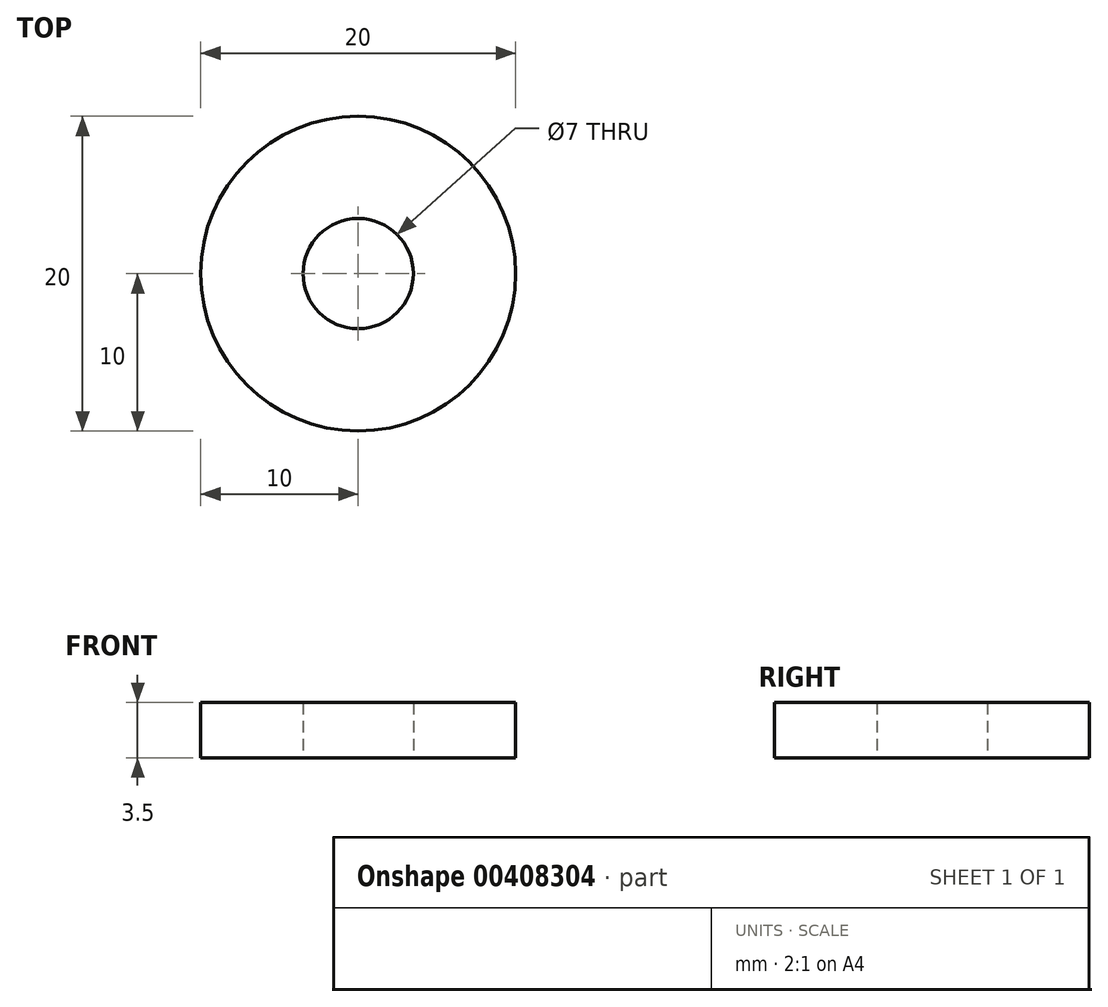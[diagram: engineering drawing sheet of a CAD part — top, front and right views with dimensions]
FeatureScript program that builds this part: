
annotation { "Feature Type Name" : "Feature", "Feature Type Description" : "" }
export const myFeature = defineFeature(function(context is Context, id is Id, definition is map)
    precondition{}
    {
        {
            var Q0;
            Q0=qCreatedBy(makeId("Top.planeOp"),FACE);
            var sketch = newSketch(context, id + "F0", { "sketchPlane" : qUnion([Q0])});
            skCircle(sketch, "E0", {"center": v(0, 0) * mm, "radius": 3.5 * mm});
            skCircle(sketch, "E1", {"center": v(0, 0) * mm, "radius": 10 * mm});
            skSolve(sketch);
        }
        {
            var Q0;
            Q0 = qSketchRegion(id + "F0", true);
            extrude(context, id + "F1", {"entities" : qUnion([Q0]), "depth" : 3.5 * mm});
        }
    });
